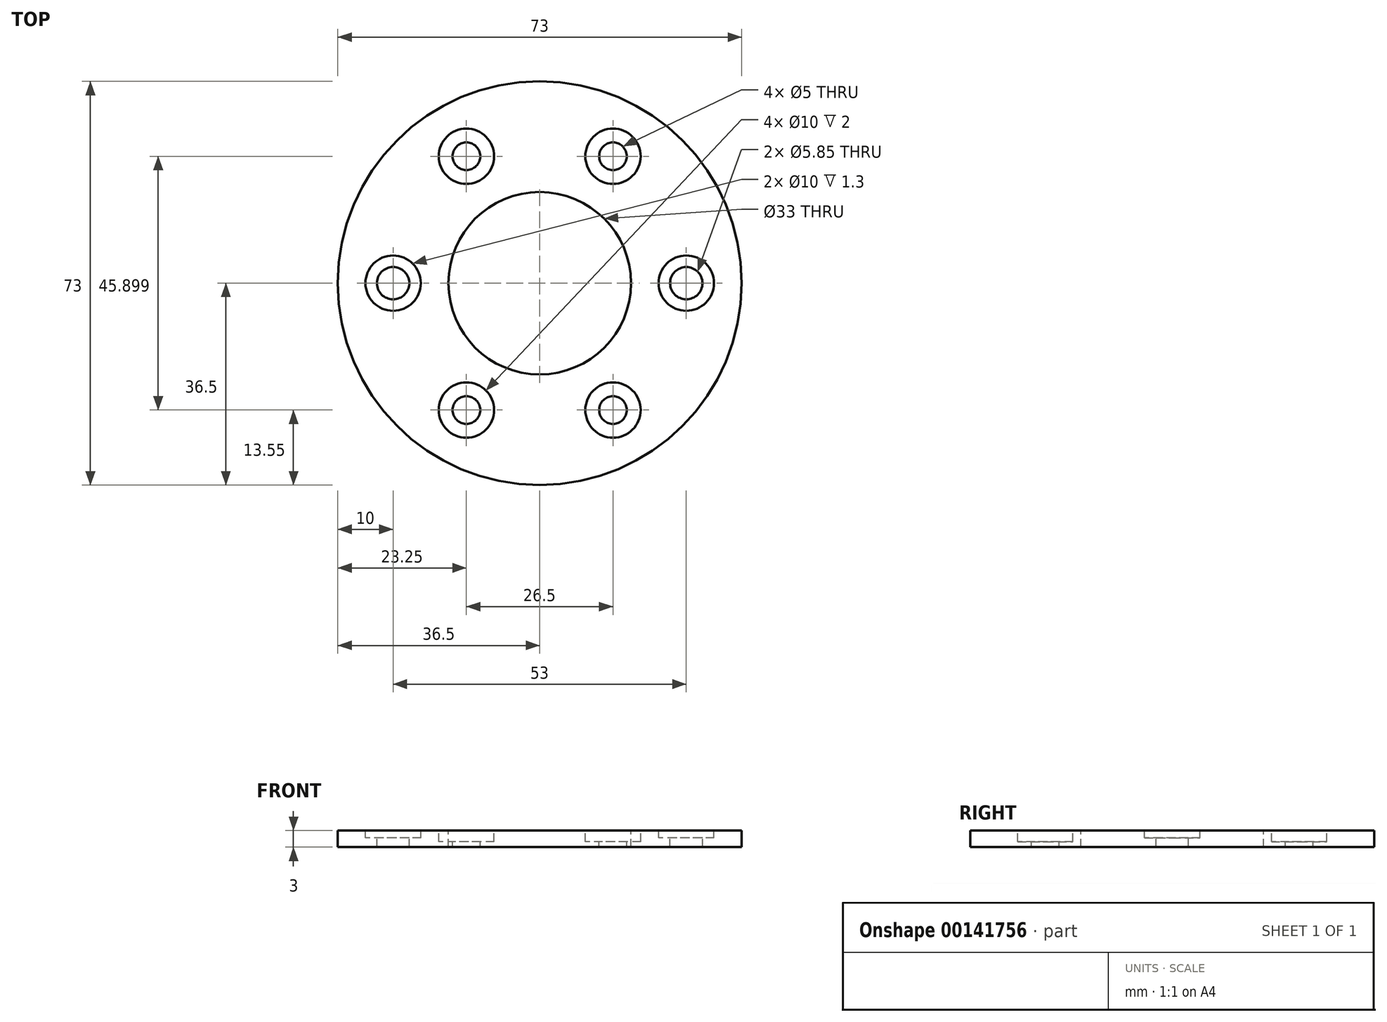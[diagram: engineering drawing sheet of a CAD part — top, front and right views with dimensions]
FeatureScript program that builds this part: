
annotation { "Feature Type Name" : "Feature", "Feature Type Description" : "" }
export const myFeature = defineFeature(function(context is Context, id is Id, definition is map)
    precondition{}
    {
        {
            var Q0;
            Q0=qCreatedBy(makeId("Top.planeOp"),FACE);
            var sketch = newSketch(context, id + "F0", { "sketchPlane" : qUnion([Q0])});
            skCircle(sketch, "E0", {"center": v(0, 0) * mm, "radius": 36.5 * mm});
            skPoint(sketch, "E1", {"position": v(-26.5, 0) * mm});
            skCircle(sketch, "E2", {"center": v(0, 0) * mm, "radius": 16.5 * mm});
            skPoint(sketch, "E3.1.0", {"position": v(-13.25, 22.95) * mm});
            skPoint(sketch, "E3.2.0", {"position": v(13.25, 22.95) * mm});
            skPoint(sketch, "E3.3.0", {"position": v(26.5, 0) * mm});
            skPoint(sketch, "E3.4.0", {"position": v(13.25, -22.95) * mm});
            skPoint(sketch, "E3.5.0", {"position": v(-13.25, -22.95) * mm});
            skLineSegment(sketch, "E3.anchor1", {"start": v(0, 0) * mm, "end": v(-26.5, 0) * mm, "construction": true});
            skLineSegment(sketch, "E3.anchor2", {"start": v(0, 0) * mm, "end": v(-13.25, -22.95) * mm, "construction": true});
            skLineSegment(sketch, "E4", {"start": v(16.5, 0) * mm, "end": v(26.5, 0) * mm, "construction": true});
            skLineSegment(sketch, "E5", {"start": v(26.5, 0) * mm, "end": v(36.5, 0) * mm, "construction": true});
            skSolve(sketch);
        }
        {
            var Q0;
            Q0=makeQuery(id+"F0.imprint","IMPRINT",FACE,{"disambiguationData":[TD([[makeQuery(id+"F0.imprint","IMPRINT",EDGE,{"derivedFrom":sQuery(id+"F0.wireOp",EDGE,"E0")}),1.0]])]});
            extrude(context, id + "F1", {"entities" : qUnion([Q0]), "oppositeDirection" : true, "depth" : 3 * mm});
        }
        {
            var Q0;
            Q0=sQuery(id+"F0.wireOp",VERTEX,"E3.1.0");
            var Q1;
            Q1=sQuery(id+"F0.wireOp",VERTEX,"E3.2.0");
            var Q2;
            Q2=sQuery(id+"F0.wireOp",VERTEX,"E3.5.0");
            var Q3;
            Q3=sQuery(id+"F0.wireOp",VERTEX,"E3.4.0");
            var Q4;
            Q4=makeQuery(id+"F1.opExtrude","SWEPT_BODY",BODY,{"disambiguationData":[OSD([sQuery(id+"F0.wireOp",EDGE,"E0")])]});
            hole(context, id + "F2", {"style" : HoleStyle.C_BORE, "endStyle" : HoleEndStyle.THROUGH, "holeDiameter" : 5 * mm, "cBoreDiameter" : 10 * mm, "cBoreDepth" : 2 * mm, "tappedDepth" : 12 * mm, "tapClearance" : 3, "locations" : qUnion([Q0, Q1, Q2, Q3]), "scope" : qUnion([Q4])});
        }
        {
            var Q0;
            Q0=sQuery(id+"F0.wireOp",VERTEX,"E1");
            var Q1;
            Q1=sQuery(id+"F0.wireOp",VERTEX,"E3.3.0");
            var Q2;
            Q2=makeQuery(id+"F1.opExtrude","SWEPT_BODY",BODY,{"disambiguationData":[OSD([sQuery(id+"F0.wireOp",EDGE,"E0")])]});
            hole(context, id + "F3", {"style" : HoleStyle.C_BORE, "endStyle" : HoleEndStyle.THROUGH, "holeDiameter" : 5.85 * mm, "cBoreDiameter" : 10 * mm, "cBoreDepth" : 1.3 * mm, "tappedDepth" : 12 * mm, "tapClearance" : 3, "locations" : qUnion([Q0, Q1]), "scope" : qUnion([Q2])});
        }
    });
